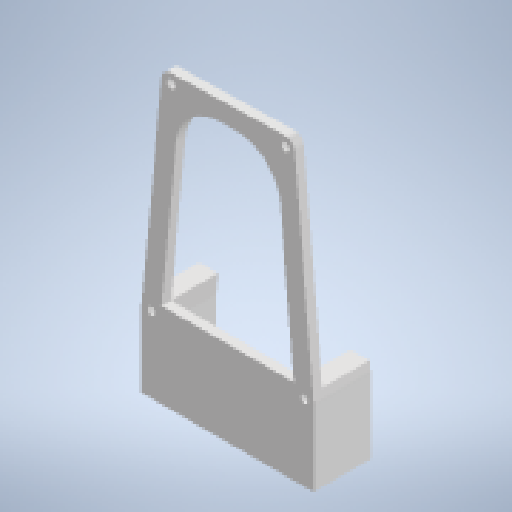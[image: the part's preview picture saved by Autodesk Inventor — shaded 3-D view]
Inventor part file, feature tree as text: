
AUTODESK INVENTOR PART (.ipt)
format: ipt  version: 2024.2 (Build 282272000, 272)  size: 277,504 bytes
history: native  units: mm
features: other x24, extrude x6, sketch x6, projected_geometry x5, fillet x1
ambient origin geometry x8: Origin, YZ Plane, XZ Plane, XY Plane, X Axis, Y Axis, Z Axis, Center Point
bodies: Solide1 (feature_tree)
feature tree (42):
  extrude  "Extrusion1"  Depth=8.0mm
  fillet  "Congé1"  Radius=8.0mm
  extrude  "Extrusion2"  Depth=8.0mm
  extrude  "Extrusion3"  Depth=8.0mm
  extrude  "Extrusion4"  Depth=4.0mm TaperAngle=0.0deg
  extrude  "Extrusion5"  Depth=19.0mm
  sketch  "Esquisse6"
  other  "Plan de construction1"
  extrude  "Extrusion6"  Depth=20.0mm TaperAngle=0.0deg
  sketch  "Esquisse1"
  other  "Référence1"
  other  "Référence2"
  other  "Référence3"
  other  "Référence4"
  other  "Référence5"
  sketch  "Esquisse2"
  projected_geometry  "Boucle projetée1"
  sketch  "Esquisse3"
  projected_geometry  "Boucle projetée2"
  projected_geometry  "Boucle projetée3"
  projected_geometry  "Boucle projetée4"
  sketch  "Esquisse4"
  projected_geometry  "Boucle projetée5"
  sketch  "Esquisse5"
  other  "Référence6"
  other  "Référence7"
  other  "Référence8"
  other  "Référence9"
  other  "Référence10"
  other  "Référence11"
  other  "Référence12"
  other  "Référence13"
  other  "Référence14"
  other  "Référence15"
  other  "<userpath>\Desktop\Robot\blocdrivermoteur.iam"
  other  "blocdrivermoteur.iam"
  other  "NUCLEO-F411RE:1"
  other  "xnucleo:1"
  other  "xucleobase:1"
  other  "<userpath>\Desktop\Robot\Robotbebou.iam"
  other  "Robotbebou.iam"
  other  "embase:1"
